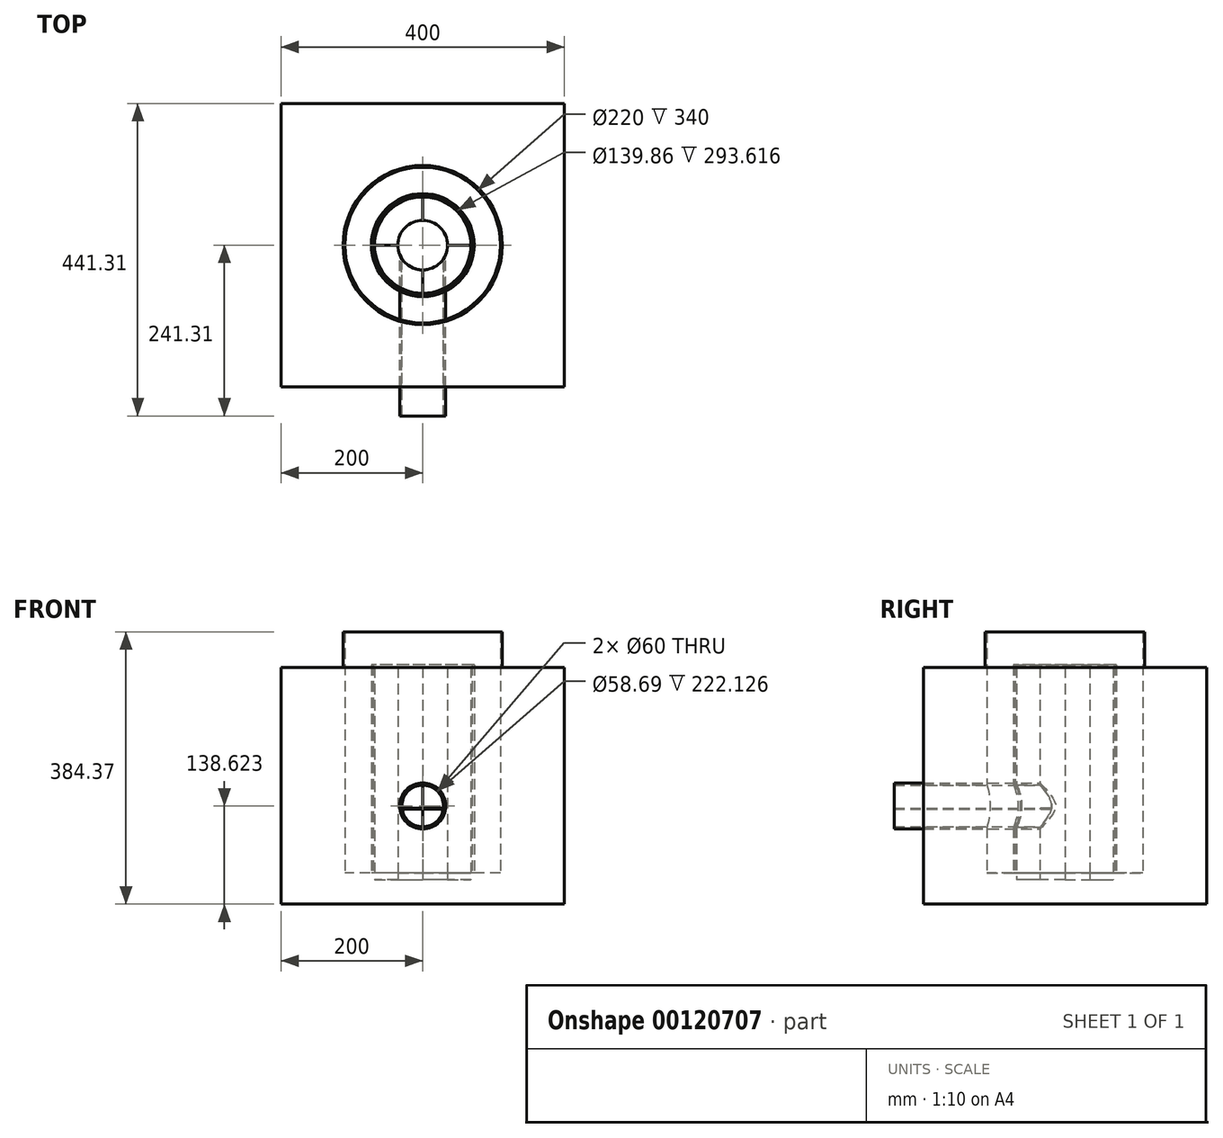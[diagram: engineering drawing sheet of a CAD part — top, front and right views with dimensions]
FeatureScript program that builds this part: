
annotation { "Feature Type Name" : "Feature", "Feature Type Description" : "" }
export const myFeature = defineFeature(function(context is Context, id is Id, definition is map)
    precondition{}
    {
        {
            var Q0;
            Q0=qCreatedBy(makeId("Top.planeOp"),FACE);
            var sketch = newSketch(context, id + "F0", { "sketchPlane" : qUnion([Q0])});
            skLineSegment(sketch, "E0.bottom", {"start": v(200, 200) * mm, "end": v(-200, 200) * mm});
            skLineSegment(sketch, "E0.top", {"start": v(200, -200) * mm, "end": v(-200, -200) * mm});
            skLineSegment(sketch, "E0.left", {"start": v(200, 200) * mm, "end": v(200, -200) * mm});
            skLineSegment(sketch, "E0.right", {"start": v(-200, 200) * mm, "end": v(-200, -200) * mm});
            skPoint(sketch, "E0.middle", {"position": v(0, 0) * mm});
            skCircle(sketch, "E1", {"center": v(0, 0) * mm, "radius": 112.5 * mm});
            skCircle(sketch, "E2", {"center": v(0, 0) * mm, "radius": 70 * mm});
            skCircle(sketch, "E3", {"center": v(0, 0) * mm, "radius": 110 * mm});
            skCircle(sketch, "E4", {"center": v(0, 0) * mm, "radius": 72.5 * mm});
            skCircle(sketch, "E5", {"center": v(0, 0) * mm, "radius": 68 * mm});
            skCircle(sketch, "E6", {"center": v(0, 0) * mm, "radius": 35 * mm});
            skLineSegment(sketch, "E7", {"start": v(0, 35) * mm, "end": v(0, 68) * mm});
            skLineSegment(sketch, "E8", {"start": v(-35, 0) * mm, "end": v(-68, 0) * mm});
            skLineSegment(sketch, "E9", {"start": v(0, -35) * mm, "end": v(0, -68) * mm});
            skLineSegment(sketch, "E10", {"start": v(35, 0) * mm, "end": v(68, 0) * mm});
            skLineSegment(sketch, "E11", {"start": v(0, -110) * mm, "end": v(0, -200) * mm, "construction": true});
            skSolve(sketch);
        }
        {
            var Q0;
            {var subQ0=sQuery(id+"F0.wireOp",EDGE,"E7");Q0=makeQuery(id+"F0.imprint","IMPRINT",FACE,{"disambiguationData":[TD([[makeQuery(id+"F0.imprint","IMPRINT",EDGE,{"derivedFrom":subQ0}),1.0]])]});}
            var Q1;
            {var subQ0=sQuery(id+"F0.wireOp",EDGE,"E9");Q1=makeQuery(id+"F0.imprint","IMPRINT",FACE,{"disambiguationData":[TD([[makeQuery(id+"F0.imprint","IMPRINT",EDGE,{"derivedFrom":subQ0}),1.0]])]});}
            extrude(context, id + "F1", {"entities" : qUnion([Q0, Q1]), "depth" : 300 * mm});
        }
        {
            var Q0;
            Q0=qCreatedBy(makeId("Top.planeOp"),FACE);
            var sketch = newSketch(context, id + "F2", { "sketchPlane" : qUnion([Q0])});
            skLineSegment(sketch, "E12.bottom", {"start": v(200, -200) * mm, "end": v(-200, -200) * mm});
            skLineSegment(sketch, "E12.top", {"start": v(200, 200) * mm, "end": v(-200, 200) * mm});
            skLineSegment(sketch, "E12.left", {"start": v(200, -200) * mm, "end": v(200, 200) * mm});
            skLineSegment(sketch, "E12.right", {"start": v(-200, -200) * mm, "end": v(-200, 200) * mm});
            skPoint(sketch, "E12.middle", {"position": v(0, 0) * mm});
            skSolve(sketch);
        }
        {
            var Q0;
            Q0=makeQuery(id+"F0.imprint","IMPRINT",FACE,{"disambiguationData":[TD([[makeQuery(id+"F0.imprint","IMPRINT",EDGE,{"derivedFrom":sQuery(id+"F0.wireOp",EDGE,"E0.bottom")}),1.0]])]});
            extrude(context, id + "F3", {"entities" : qUnion([Q0]), "depth" : 300 * mm});
        }
        {
            var Q0;
            Q0=qCreatedBy(makeId("Front.planeOp"),FACE);
            var sketch = newSketch(context, id + "F4", { "sketchPlane" : qUnion([Q0])});
            skLineSegment(sketch, "E13.0", {"start": v(200, 0) * mm, "end": v(-200, 0) * mm});
            skLineSegment(sketch, "E14.0", {"start": v(-200, 300) * mm, "end": v(-200, 0) * mm, "construction": true});
            skPoint(sketch, "E15.0", {"position": v(0, 0) * mm});
            skLineSegment(sketch, "E16.0", {"start": v(200, 0) * mm, "end": v(-200, 0) * mm, "construction": true});
            skLineSegment(sketch, "E17", {"start": v(-200, 300) * mm, "end": v(199.86, 300) * mm, "construction": true});
            skLineSegment(sketch, "E18", {"start": v(0, 0) * mm, "end": v(0, 300) * mm, "construction": true});
            skCircle(sketch, "E19.0", {"center": v(0, 104.25) * mm, "radius": 30 * mm});
            skSolve(sketch);
        }
        {
            var Q0;
            Q0=makeQuery(id+"F3.opExtrude","SWEPT_FACE",FACE,{"disambiguationData":[OSD([sQuery(id+"F0.wireOp",EDGE,"E0.top")])]});
            var sketch = newSketch(context, id + "F5", { "sketchPlane" : qUnion([Q0])});
            skLineSegment(sketch, "E20", {"start": v(0, 0) * mm, "end": v(0, 300) * mm, "construction": true});
            skCircle(sketch, "E21", {"center": v(0, 103.54) * mm, "radius": 30.17 * mm});
            skSolve(sketch);
        }
        {
            var Q0;
            Q0=makeQuery(id+"F0.imprint","IMPRINT",FACE,{"disambiguationData":[TD([[makeQuery(id+"F0.imprint","IMPRINT",EDGE,{"derivedFrom":sQuery(id+"F0.wireOp",EDGE,"E1")}),1.0]])]});
            var Q1;
            Q1=sQuery(id+"F0.wireOp",EDGE,"E3");
            var Q2;
            Q2=sQuery(id+"F0.wireOp",EDGE,"E1");
            extrude(context, id + "F6", {"entities" : qUnion([Q0]), "surfaceEntities" : qUnion([Q1, Q2]), "depth" : 350 * mm});
        }
        {
            var Q0;
            Q0 = qSketchRegion(id + "F2", true);
            extrude(context, id + "F7", {"entities" : qUnion([Q0]), "operationType" : NewBodyOperationType.ADD, "depth" : 10 * mm, "hasSecondDirection" : true, "secondDirectionOppositeDirection" : true, "secondDirectionDepth" : 34.37 * mm});
        }
        {
            var Q0;
            {var subQ0=sQuery(id+"F0.wireOp",EDGE,"E8");Q0=makeQuery(id+"F0.imprint","IMPRINT",FACE,{"disambiguationData":[TD([[makeQuery(id+"F0.imprint","IMPRINT",EDGE,{"derivedFrom":subQ0}),1.0]])]});}
            var Q1;
            {var subQ0=sQuery(id+"F0.wireOp",EDGE,"E7");Q1=makeQuery(id+"F0.imprint","IMPRINT",FACE,{"disambiguationData":[TD([[makeQuery(id+"F0.imprint","IMPRINT",EDGE,{"derivedFrom":subQ0}),-1.0]])]});}
            extrude(context, id + "F8", {"entities" : qUnion([Q0, Q1]), "depth" : 300 * mm});
        }
        {
            var Q0;
            Q0=makeQuery(id+"F7.opExtrude","CAP_FACE",FACE,{"disambiguationData":[OSD([sQuery(id+"F2.wireOp",EDGE,"E12.bottom"),sQuery(id+"F2.wireOp",EDGE,"E12.top"),sQuery(id+"F2.wireOp",EDGE,"E12.left"),sQuery(id+"F2.wireOp",EDGE,"E12.right")])],"isStart":false});
            var sketch = newSketch(context, id + "F9", { "sketchPlane" : qUnion([Q0])});
            skCircle(sketch, "E22", {"center": v(0, 0) * mm, "radius": 72.74 * mm});
            skCircle(sketch, "E23", {"center": v(0, 0) * mm, "radius": 69.93 * mm});
            skSolve(sketch);
        }
        {
            var Q0;
            Q0=makeQuery(id+"F9.imprint","IMPRINT",FACE,{"disambiguationData":[TD([[makeQuery(id+"F9.imprint","IMPRINT",EDGE,{"derivedFrom":sQuery(id+"F9.wireOp",EDGE,"E22")}),1.0]])]});
            extrude(context, id + "F10", {"entities" : qUnion([Q0]), "operationType" : NewBodyOperationType.ADD, "depth" : 293.62 * mm});
        }
        {
            var Q0;
            Q0 = qSketchRegion(id + "F4", true);
            var Q1;
            Q1=sQuery(id+"F4.wireOp",EDGE,"E19.0");
            var Q2;
            Q2=sQuery(id+"F4.wireOp",EDGE,"09TM6k92-Xy9Z-1SVS-R73X-6XhNFsHiQCwU");
            extrude(context, id + "F11", {"entities" : qUnion([Q0]), "operationType" : NewBodyOperationType.REMOVE, "surfaceEntities" : qUnion([Q1, Q2]), "endBound" : BoundingType.THROUGH_ALL, "depth" : 230 * mm});
        }
        {
            var Q0;
            Q0=makeQuery(id+"F5.imprint","IMPRINT",FACE,{"disambiguationData":[TD([[makeQuery(id+"F5.imprint","IMPRINT",EDGE,{"derivedFrom":sQuery(id+"F5.wireOp",EDGE,"E21")}),-1.0]])]});
            var sketch = newSketch(context, id + "F12", { "sketchPlane" : qUnion([Q0])});
            skCircle(sketch, "E24", {"center": v(0, 104.25) * mm, "radius": 32.62 * mm});
            skCircle(sketch, "E25", {"center": v(0, 104.25) * mm, "radius": 29.34 * mm});
            skSolve(sketch);
        }
        {
            var Q0;
            Q0 = qSketchRegion(id + "F12", true);
            extrude(context, id + "F13", {"entities" : qUnion([Q0]), "depth" : 41.3 * mm, "hasSecondDirection" : true, "secondDirectionOppositeDirection" : true, "secondDirectionDepth" : 188.14 * mm});
        }
        {
            var Q0;
            Q0=makeQuery(id+"F5.imprint","IMPRINT",FACE,{"disambiguationData":[TD([[makeQuery(id+"F5.imprint","IMPRINT",EDGE,{"derivedFrom":sQuery(id+"F5.wireOp",EDGE,"E21")}),-1.0]])]});
            var sketch = newSketch(context, id + "F14", { "sketchPlane" : qUnion([Q0])});
            skCircle(sketch, "E26.0", {"center": v(0, 104.25) * mm, "radius": 29.34 * mm, "construction": true});
            skLineSegment(sketch, "E27", {"start": v(-29.17, 101.12) * mm, "end": v(29.17, 101.12) * mm});
            skLineSegment(sketch, "E28", {"start": v(29.17, 101.12) * mm, "end": v(29.05, 100.13) * mm});
            skLineSegment(sketch, "E29", {"start": v(29.05, 100.13) * mm, "end": v(-29.05, 100.13) * mm});
            skLineSegment(sketch, "E30", {"start": v(-29.05, 100.13) * mm, "end": v(-29.17, 101.12) * mm});
            skSolve(sketch);
        }
        {
            var Q0;
            Q0 = qSketchRegion(id + "F14", true);
            var Q1;
            Q1=makeQuery(id+"F13.opExtrude","CAP_FACE",FACE,{"disambiguationData":[OSD([sQuery(id+"F12.wireOp",EDGE,"E24"),sQuery(id+"F12.wireOp",EDGE,"E25")])],"isStart":false});
            extrude(context, id + "F15", {"entities" : qUnion([Q0]), "endBound" : BoundingType.UP_TO_SURFACE, "endBoundEntityFace" : qUnion([Q1]), "depth" : 35.81 * mm, "hasSecondDirection" : true, "secondDirectionOppositeDirection" : true, "secondDirectionDepth" : 187.08 * mm});
        }
        {
            var Q0;
            Q0=makeQuery(id+"F10.boolean.opBoolean","SPLIT",FACE,{"disambiguationData":[TD([makeQuery(id+"F10.opExtrude","SWEPT_FACE",FACE,{"disambiguationData":[OSD([sQuery(id+"F9.wireOp",EDGE,"E23")])]})])],"derivedFrom":makeQuery(id+"F7.opExtrude","CAP_FACE",FACE,{"disambiguationData":[OSD([sQuery(id+"F2.wireOp",EDGE,"E12.bottom"),sQuery(id+"F2.wireOp",EDGE,"E12.top"),sQuery(id+"F2.wireOp",EDGE,"E12.left"),sQuery(id+"F2.wireOp",EDGE,"E12.right")])],"isStart":false})});
            var sketch = newSketch(context, id + "F16", { "sketchPlane" : qUnion([Q0])});
            skCircle(sketch, "E31", {"center": v(0, 0) * mm, "radius": 35.06 * mm});
            skSolve(sketch);
        }
        {
            var Q0;
            Q0 = qSketchRegion(id + "F16", true);
            extrude(context, id + "F17", {"entities" : qUnion([Q0]), "operationType" : NewBodyOperationType.REMOVE, "depth" : 410.93 * mm});
        }
    });
